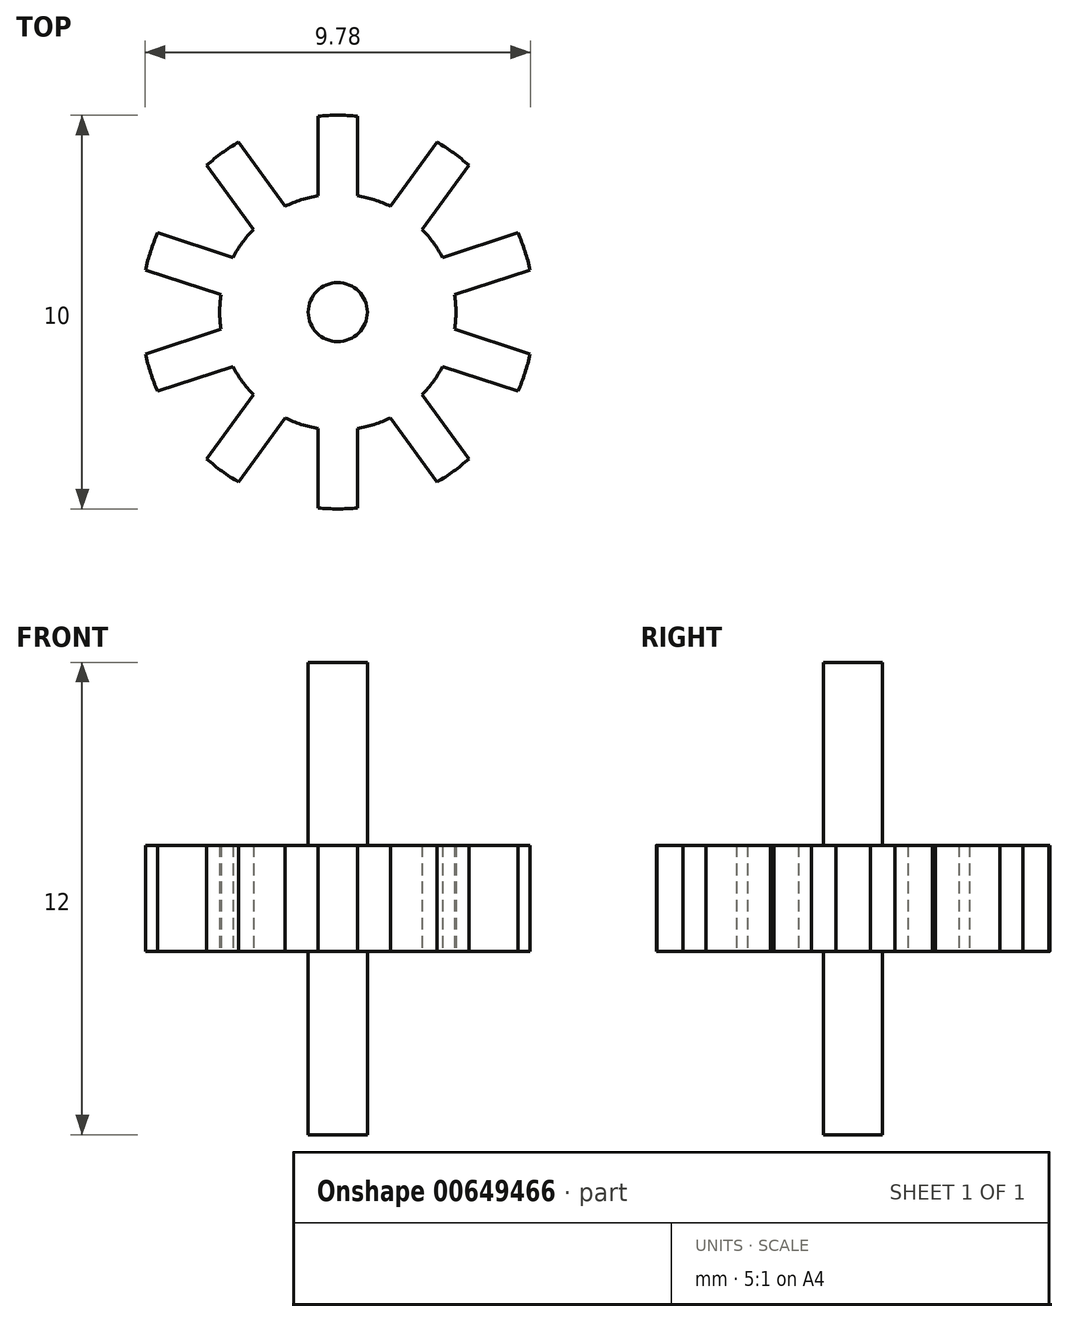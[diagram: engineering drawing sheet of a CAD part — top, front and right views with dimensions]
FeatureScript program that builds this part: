
annotation { "Feature Type Name" : "Feature", "Feature Type Description" : "" }
export const myFeature = defineFeature(function(context is Context, id is Id, definition is map)
    precondition{}
    {
        {
            var Q0;
            Q0=qCreatedBy(makeId("Top.planeOp"),FACE);
            var sketch = newSketch(context, id + "F0", { "sketchPlane" : qUnion([Q0])});
            skCircle(sketch, "E0", {"center": v(0, 0) * mm, "radius": 3 * mm});
            skLineSegment(sketch, "E1.bottom", {"start": v(0.5, 6) * mm, "end": v(-0.5, 6) * mm});
            skLineSegment(sketch, "E1.top", {"start": v(0.5, 0) * mm, "end": v(-0.5, 0) * mm});
            skLineSegment(sketch, "E1.left", {"start": v(0.5, 6) * mm, "end": v(0.5, 0) * mm});
            skLineSegment(sketch, "E1.right", {"start": v(-0.5, 6) * mm, "end": v(-0.5, 0) * mm});
            skPoint(sketch, "E1.middle", {"position": v(0, 3) * mm});
            skLineSegment(sketch, "E2.1.0", {"start": v(-3.12, 5.15) * mm, "end": v(-3.93, 4.56) * mm});
            skLineSegment(sketch, "E2.1.1", {"start": v(-3.93, 4.56) * mm, "end": v(-0.4, -0.3) * mm});
            skLineSegment(sketch, "E2.1.2", {"start": v(-3.12, 5.15) * mm, "end": v(0.4, 0.3) * mm});
            skLineSegment(sketch, "E2.2.0", {"start": v(-5.55, 2.33) * mm, "end": v(-5.86, 1.38) * mm});
            skLineSegment(sketch, "E2.2.1", {"start": v(-5.86, 1.38) * mm, "end": v(-0.15, -0.48) * mm});
            skLineSegment(sketch, "E2.2.2", {"start": v(-5.55, 2.33) * mm, "end": v(0.15, 0.48) * mm});
            skLineSegment(sketch, "E2.3.0", {"start": v(-5.86, -1.38) * mm, "end": v(-5.55, -2.33) * mm});
            skLineSegment(sketch, "E2.3.1", {"start": v(-5.55, -2.33) * mm, "end": v(0.15, -0.48) * mm});
            skLineSegment(sketch, "E2.3.2", {"start": v(-5.86, -1.38) * mm, "end": v(-0.15, 0.48) * mm});
            skLineSegment(sketch, "E2.4.0", {"start": v(-3.93, -4.56) * mm, "end": v(-3.12, -5.15) * mm});
            skLineSegment(sketch, "E2.4.1", {"start": v(-3.12, -5.15) * mm, "end": v(0.4, -0.3) * mm});
            skLineSegment(sketch, "E2.4.2", {"start": v(-3.93, -4.56) * mm, "end": v(-0.4, 0.3) * mm});
            skLineSegment(sketch, "E2.5.0", {"start": v(-0.5, -6) * mm, "end": v(0.5, -6) * mm});
            skLineSegment(sketch, "E2.5.1", {"start": v(0.5, -6) * mm, "end": v(0.5, 0) * mm});
            skLineSegment(sketch, "E2.5.2", {"start": v(-0.5, -6) * mm, "end": v(-0.5, 0) * mm});
            skLineSegment(sketch, "E2.6.0", {"start": v(3.12, -5.15) * mm, "end": v(3.93, -4.56) * mm});
            skLineSegment(sketch, "E2.6.1", {"start": v(3.93, -4.56) * mm, "end": v(0.4, 0.3) * mm});
            skLineSegment(sketch, "E2.6.2", {"start": v(3.12, -5.15) * mm, "end": v(-0.4, -0.3) * mm});
            skLineSegment(sketch, "E2.7.0", {"start": v(5.55, -2.33) * mm, "end": v(5.86, -1.38) * mm});
            skLineSegment(sketch, "E2.7.1", {"start": v(5.86, -1.38) * mm, "end": v(0.15, 0.48) * mm});
            skLineSegment(sketch, "E2.7.2", {"start": v(5.55, -2.33) * mm, "end": v(-0.15, -0.48) * mm});
            skLineSegment(sketch, "E2.8.0", {"start": v(5.86, 1.38) * mm, "end": v(5.55, 2.33) * mm});
            skLineSegment(sketch, "E2.8.1", {"start": v(5.55, 2.33) * mm, "end": v(-0.15, 0.48) * mm});
            skLineSegment(sketch, "E2.8.2", {"start": v(5.86, 1.38) * mm, "end": v(0.15, -0.48) * mm});
            skLineSegment(sketch, "E2.9.0", {"start": v(3.93, 4.56) * mm, "end": v(3.12, 5.15) * mm});
            skLineSegment(sketch, "E2.9.1", {"start": v(3.12, 5.15) * mm, "end": v(-0.4, 0.3) * mm});
            skLineSegment(sketch, "E2.9.2", {"start": v(3.93, 4.56) * mm, "end": v(0.4, -0.3) * mm});
            skCircle(sketch, "E3", {"center": v(0, 0) * mm, "radius": 0.5 * mm});
            skCircle(sketch, "E4", {"center": v(0, 0) * mm, "radius": 5 * mm});
            skSolve(sketch);
        }
        {
            var Q0;
            {var subQ0=sQuery(id+"F0.wireOp",EDGE,"E2.3.2");var subQ1=sQuery(id+"F0.wireOp",EDGE,"E0");var subQ2=makeQuery(id+"F0.imprint","INTERSECT",VERTEX,{"derivedFrom":[subQ1,subQ0]});Q0=makeQuery(id+"F0.imprint","IMPRINT",FACE,{"disambiguationData":[TD([[makeQuery(id+"F0.imprint","IMPRINT",EDGE,{"disambiguationData":[TD([[subQ2,-1.0]])],"derivedFrom":subQ1}),1.0]])]});}
            var Q1;
            {var subQ0=sQuery(id+"F0.wireOp",EDGE,"E2.6.1");var subQ1=sQuery(id+"F0.wireOp",EDGE,"E0");var subQ2=makeQuery(id+"F0.imprint","INTERSECT",VERTEX,{"derivedFrom":[subQ1,subQ0]});Q1=makeQuery(id+"F0.imprint","IMPRINT",FACE,{"disambiguationData":[TD([[makeQuery(id+"F0.imprint","IMPRINT",EDGE,{"disambiguationData":[TD([[subQ2,-1.0]])],"derivedFrom":subQ1}),1.0]])]});}
            var Q2;
            {var subQ0=sQuery(id+"F0.wireOp",EDGE,"E2.4.2");var subQ1=sQuery(id+"F0.wireOp",EDGE,"E0");var subQ2=makeQuery(id+"F0.imprint","INTERSECT",VERTEX,{"derivedFrom":[subQ1,subQ0]});Q2=makeQuery(id+"F0.imprint","IMPRINT",FACE,{"disambiguationData":[TD([[makeQuery(id+"F0.imprint","IMPRINT",EDGE,{"disambiguationData":[TD([[subQ2,-1.0]])],"derivedFrom":subQ1}),1.0]])]});}
            var Q3;
            {var subQ0=sQuery(id+"F0.wireOp",EDGE,"E2.7.1");var subQ1=sQuery(id+"F0.wireOp",EDGE,"E1.left");var subQ2=makeQuery(id+"F0.imprint","INTERSECT",VERTEX,{"derivedFrom":[subQ1,subQ0]});Q3=makeQuery(id+"F0.imprint","IMPRINT",FACE,{"disambiguationData":[TD([[makeQuery(id+"F0.imprint","IMPRINT",EDGE,{"disambiguationData":[TD([[subQ2,-1.0]])],"derivedFrom":subQ1}),1.0]])]});}
            var Q4;
            {var subQ0=sQuery(id+"F0.wireOp",EDGE,"E2.5.1");var subQ1=sQuery(id+"F0.wireOp",EDGE,"E0");var subQ2=makeQuery(id+"F0.imprint","INTERSECT",VERTEX,{"derivedFrom":[subQ1,subQ0]});Q4=makeQuery(id+"F0.imprint","IMPRINT",FACE,{"disambiguationData":[TD([[makeQuery(id+"F0.imprint","IMPRINT",EDGE,{"disambiguationData":[TD([[subQ2,-1.0]])],"derivedFrom":subQ1}),1.0]])]});}
            var Q5;
            {var subQ4=sQuery(id+"F0.wireOp",EDGE,"E1.top");Q5=makeQuery(id+"F0.imprint","IMPRINT",FACE,{"disambiguationData":[TD([[makeQuery(id+"F0.imprint","IMPRINT",EDGE,{"derivedFrom":subQ4}),1.0]])]});}
            var Q6;
            {var subQ0=sQuery(id+"F0.wireOp",EDGE,"E2.3.2");var subQ1=sQuery(id+"F0.wireOp",EDGE,"E1.right");var subQ2=makeQuery(id+"F0.imprint","INTERSECT",VERTEX,{"derivedFrom":[subQ1,subQ0]});Q6=makeQuery(id+"F0.imprint","IMPRINT",FACE,{"disambiguationData":[TD([[makeQuery(id+"F0.imprint","IMPRINT",EDGE,{"disambiguationData":[TD([[subQ2,-1.0]])],"derivedFrom":subQ1}),-1.0]])]});}
            var Q7;
            {var subQ0=sQuery(id+"F0.wireOp",EDGE,"E2.7.2");var subQ1=sQuery(id+"F0.wireOp",EDGE,"E2.4.1");var subQ2=makeQuery(id+"F0.imprint","INTERSECT",VERTEX,{"derivedFrom":[subQ1,subQ0]});Q7=makeQuery(id+"F0.imprint","IMPRINT",FACE,{"disambiguationData":[TD([[makeQuery(id+"F0.imprint","IMPRINT",EDGE,{"disambiguationData":[TD([[subQ2,-1.0]])],"derivedFrom":subQ1}),-1.0]])]});}
            var Q8;
            {var subQ0=sQuery(id+"F0.wireOp",EDGE,"E1.right");var subQ1=sQuery(id+"F0.wireOp",EDGE,"E0");var subQ2=makeQuery(id+"F0.imprint","INTERSECT",VERTEX,{"derivedFrom":[subQ1,subQ0]});Q8=makeQuery(id+"F0.imprint","IMPRINT",FACE,{"disambiguationData":[TD([[makeQuery(id+"F0.imprint","IMPRINT",EDGE,{"disambiguationData":[TD([[subQ2,-1.0]])],"derivedFrom":subQ1}),1.0]])]});}
            var Q9;
            {var subQ0=sQuery(id+"F0.wireOp",EDGE,"E2.9.1");var subQ1=sQuery(id+"F0.wireOp",EDGE,"E0");var subQ2=makeQuery(id+"F0.imprint","INTERSECT",VERTEX,{"derivedFrom":[subQ1,subQ0]});Q9=makeQuery(id+"F0.imprint","IMPRINT",FACE,{"disambiguationData":[TD([[makeQuery(id+"F0.imprint","IMPRINT",EDGE,{"disambiguationData":[TD([[subQ2,-1.0]])],"derivedFrom":subQ1}),1.0]])]});}
            var Q10;
            {var subQ0=sQuery(id+"F0.wireOp",EDGE,"E2.8.1");var subQ1=sQuery(id+"F0.wireOp",EDGE,"E0");var subQ2=makeQuery(id+"F0.imprint","INTERSECT",VERTEX,{"derivedFrom":[subQ1,subQ0]});Q10=makeQuery(id+"F0.imprint","IMPRINT",FACE,{"disambiguationData":[TD([[makeQuery(id+"F0.imprint","IMPRINT",EDGE,{"disambiguationData":[TD([[subQ2,-1.0]])],"derivedFrom":subQ1}),1.0]])]});}
            var Q11;
            {var subQ0=sQuery(id+"F0.wireOp",EDGE,"E2.8.1");var subQ1=sQuery(id+"F0.wireOp",EDGE,"E1.left");var subQ2=makeQuery(id+"F0.imprint","INTERSECT",VERTEX,{"derivedFrom":[subQ1,subQ0]});Q11=makeQuery(id+"F0.imprint","IMPRINT",FACE,{"disambiguationData":[TD([[makeQuery(id+"F0.imprint","IMPRINT",EDGE,{"disambiguationData":[TD([[subQ2,-1.0]])],"derivedFrom":subQ1}),1.0]])]});}
            var Q12;
            {var subQ0=sQuery(id+"F0.wireOp",EDGE,"E2.5.2");var subQ1=sQuery(id+"F0.wireOp",EDGE,"E2.2.1");var subQ2=makeQuery(id+"F0.imprint","INTERSECT",VERTEX,{"derivedFrom":[subQ1,subQ0]});Q12=makeQuery(id+"F0.imprint","IMPRINT",FACE,{"disambiguationData":[TD([[makeQuery(id+"F0.imprint","IMPRINT",EDGE,{"disambiguationData":[TD([[subQ2,-1.0]])],"derivedFrom":subQ1}),-1.0]])]});}
            var Q13;
            {var subQ0=sQuery(id+"F0.wireOp",EDGE,"E2.2.2");var subQ1=sQuery(id+"F0.wireOp",EDGE,"E0");var subQ2=makeQuery(id+"F0.imprint","INTERSECT",VERTEX,{"derivedFrom":[subQ1,subQ0]});Q13=makeQuery(id+"F0.imprint","IMPRINT",FACE,{"disambiguationData":[TD([[makeQuery(id+"F0.imprint","IMPRINT",EDGE,{"disambiguationData":[TD([[subQ2,-1.0]])],"derivedFrom":subQ1}),1.0]])]});}
            var Q14;
            {var subQ0=sQuery(id+"F0.wireOp",EDGE,"E2.2.1");var subQ1=sQuery(id+"F0.wireOp",EDGE,"E0");var subQ2=makeQuery(id+"F0.imprint","INTERSECT",VERTEX,{"derivedFrom":[subQ1,subQ0]});Q14=makeQuery(id+"F0.imprint","IMPRINT",FACE,{"disambiguationData":[TD([[makeQuery(id+"F0.imprint","IMPRINT",EDGE,{"disambiguationData":[TD([[subQ2,-1.0]])],"derivedFrom":subQ1}),1.0]])]});}
            var Q15;
            {var subQ0=sQuery(id+"F0.wireOp",EDGE,"E2.4.1");var subQ1=sQuery(id+"F0.wireOp",EDGE,"E0");var subQ2=makeQuery(id+"F0.imprint","INTERSECT",VERTEX,{"derivedFrom":[subQ1,subQ0]});Q15=makeQuery(id+"F0.imprint","IMPRINT",FACE,{"disambiguationData":[TD([[makeQuery(id+"F0.imprint","IMPRINT",EDGE,{"disambiguationData":[TD([[subQ2,-1.0]])],"derivedFrom":subQ1}),1.0]])]});}
            var Q16;
            {var subQ0=sQuery(id+"F0.wireOp",EDGE,"E2.1.1");var subQ1=sQuery(id+"F0.wireOp",EDGE,"E0");var subQ2=makeQuery(id+"F0.imprint","INTERSECT",VERTEX,{"derivedFrom":[subQ1,subQ0]});Q16=makeQuery(id+"F0.imprint","IMPRINT",FACE,{"disambiguationData":[TD([[makeQuery(id+"F0.imprint","IMPRINT",EDGE,{"disambiguationData":[TD([[subQ2,-1.0]])],"derivedFrom":subQ1}),1.0]])]});}
            var Q17;
            {var subQ0=sQuery(id+"F0.wireOp",EDGE,"E2.3.1");var subQ1=sQuery(id+"F0.wireOp",EDGE,"E0");var subQ2=makeQuery(id+"F0.imprint","INTERSECT",VERTEX,{"derivedFrom":[subQ1,subQ0]});Q17=makeQuery(id+"F0.imprint","IMPRINT",FACE,{"disambiguationData":[TD([[makeQuery(id+"F0.imprint","IMPRINT",EDGE,{"disambiguationData":[TD([[subQ2,-1.0]])],"derivedFrom":subQ1}),1.0]])]});}
            var Q18;
            {var subQ0=sQuery(id+"F0.wireOp",EDGE,"E2.2.2");var subQ1=sQuery(id+"F0.wireOp",EDGE,"E1.right");var subQ2=makeQuery(id+"F0.imprint","INTERSECT",VERTEX,{"derivedFrom":[subQ1,subQ0]});Q18=makeQuery(id+"F0.imprint","IMPRINT",FACE,{"disambiguationData":[TD([[makeQuery(id+"F0.imprint","IMPRINT",EDGE,{"disambiguationData":[TD([[subQ2,-1.0]])],"derivedFrom":subQ1}),1.0]])]});}
            var Q19;
            {var subQ0=sQuery(id+"F0.wireOp",EDGE,"E2.6.2");var subQ1=sQuery(id+"F0.wireOp",EDGE,"E2.4.1");var subQ2=makeQuery(id+"F0.imprint","INTERSECT",VERTEX,{"derivedFrom":[subQ1,subQ0]});Q19=makeQuery(id+"F0.imprint","IMPRINT",FACE,{"disambiguationData":[TD([[makeQuery(id+"F0.imprint","IMPRINT",EDGE,{"disambiguationData":[TD([[subQ2,-1.0]])],"derivedFrom":subQ1}),-1.0]])]});}
            var Q20;
            {var subQ4=sQuery(id+"F0.wireOp",EDGE,"E1.top");Q20=makeQuery(id+"F0.imprint","IMPRINT",FACE,{"disambiguationData":[TD([[makeQuery(id+"F0.imprint","IMPRINT",EDGE,{"derivedFrom":subQ4}),-1.0]])]});}
            var Q21;
            {var subQ1=sQuery(id+"F0.wireOp",EDGE,"E0");var subQ5=sQuery(id+"F0.wireOp",EDGE,"E2.8.1");var subQ6=makeQuery(id+"F0.imprint","INTERSECT",VERTEX,{"derivedFrom":[subQ1,subQ5]});Q21=makeQuery(id+"F0.imprint","IMPRINT",FACE,{"disambiguationData":[TD([[makeQuery(id+"F0.imprint","IMPRINT",EDGE,{"disambiguationData":[TD([[subQ6,1.0]])],"derivedFrom":subQ1}),1.0]])]});}
            var Q22;
            {var subQ0=sQuery(id+"F0.wireOp",EDGE,"E2.9.1");var subQ1=sQuery(id+"F0.wireOp",EDGE,"E1.left");var subQ2=makeQuery(id+"F0.imprint","INTERSECT",VERTEX,{"derivedFrom":[subQ1,subQ0]});Q22=makeQuery(id+"F0.imprint","IMPRINT",FACE,{"disambiguationData":[TD([[makeQuery(id+"F0.imprint","IMPRINT",EDGE,{"disambiguationData":[TD([[subQ2,-1.0]])],"derivedFrom":subQ1}),-1.0]])]});}
            var Q23;
            {var subQ0=sQuery(id+"F0.wireOp",EDGE,"E2.2.2");var subQ1=sQuery(id+"F0.wireOp",EDGE,"E1.right");var subQ2=makeQuery(id+"F0.imprint","INTERSECT",VERTEX,{"derivedFrom":[subQ1,subQ0]});Q23=makeQuery(id+"F0.imprint","IMPRINT",FACE,{"disambiguationData":[TD([[makeQuery(id+"F0.imprint","IMPRINT",EDGE,{"disambiguationData":[TD([[subQ2,-1.0]])],"derivedFrom":subQ1}),-1.0]])]});}
            var Q24;
            {var subQ5=sQuery(id+"F0.wireOp",EDGE,"E0");var subQ7=sQuery(id+"F0.wireOp",EDGE,"E1.left");var subQ8=makeQuery(id+"F0.imprint","INTERSECT",VERTEX,{"derivedFrom":[subQ5,subQ7]});Q24=makeQuery(id+"F0.imprint","IMPRINT",FACE,{"disambiguationData":[TD([[makeQuery(id+"F0.imprint","IMPRINT",EDGE,{"disambiguationData":[TD([[subQ8,-1.0]])],"derivedFrom":subQ5}),1.0]])]});}
            var Q25;
            {var subQ0=sQuery(id+"F0.wireOp",EDGE,"E2.7.2");var subQ1=sQuery(id+"F0.wireOp",EDGE,"E0");var subQ2=makeQuery(id+"F0.imprint","INTERSECT",VERTEX,{"derivedFrom":[subQ1,subQ0]});Q25=makeQuery(id+"F0.imprint","IMPRINT",FACE,{"disambiguationData":[TD([[makeQuery(id+"F0.imprint","IMPRINT",EDGE,{"disambiguationData":[TD([[subQ2,-1.0]])],"derivedFrom":subQ1}),1.0]])]});}
            var Q26;
            {var subQ0=sQuery(id+"F0.wireOp",EDGE,"E2.4.2");var subQ1=sQuery(id+"F0.wireOp",EDGE,"E2.1.1");var subQ2=makeQuery(id+"F0.imprint","INTERSECT",VERTEX,{"derivedFrom":[subQ1,subQ0]});Q26=makeQuery(id+"F0.imprint","IMPRINT",FACE,{"disambiguationData":[TD([[makeQuery(id+"F0.imprint","IMPRINT",EDGE,{"disambiguationData":[TD([[subQ2,-1.0]])],"derivedFrom":subQ1}),-1.0]])]});}
            var Q27;
            {var subQ0=sQuery(id+"F0.wireOp",EDGE,"E2.8.2");var subQ1=sQuery(id+"F0.wireOp",EDGE,"E2.6.1");var subQ2=makeQuery(id+"F0.imprint","INTERSECT",VERTEX,{"derivedFrom":[subQ1,subQ0]});Q27=makeQuery(id+"F0.imprint","IMPRINT",FACE,{"disambiguationData":[TD([[makeQuery(id+"F0.imprint","IMPRINT",EDGE,{"disambiguationData":[TD([[subQ2,-1.0]])],"derivedFrom":subQ1}),-1.0]])]});}
            var Q28;
            {var subQ0=sQuery(id+"F0.wireOp",EDGE,"E2.1.2");var subQ1=sQuery(id+"F0.wireOp",EDGE,"E1.right");var subQ2=makeQuery(id+"F0.imprint","INTERSECT",VERTEX,{"derivedFrom":[subQ1,subQ0]});Q28=makeQuery(id+"F0.imprint","IMPRINT",FACE,{"disambiguationData":[TD([[makeQuery(id+"F0.imprint","IMPRINT",EDGE,{"disambiguationData":[TD([[subQ2,-1.0]])],"derivedFrom":subQ1}),1.0]])]});}
            var Q29;
            {var subQ0=sQuery(id+"F0.wireOp",EDGE,"E2.6.2");var subQ1=sQuery(id+"F0.wireOp",EDGE,"E2.3.1");var subQ2=makeQuery(id+"F0.imprint","INTERSECT",VERTEX,{"derivedFrom":[subQ1,subQ0]});Q29=makeQuery(id+"F0.imprint","IMPRINT",FACE,{"disambiguationData":[TD([[makeQuery(id+"F0.imprint","IMPRINT",EDGE,{"disambiguationData":[TD([[subQ2,-1.0]])],"derivedFrom":subQ1}),-1.0]])]});}
            var Q30;
            {var subQ0=sQuery(id+"F0.wireOp",EDGE,"E2.9.1");var subQ1=sQuery(id+"F0.wireOp",EDGE,"E2.1.2");var subQ2=makeQuery(id+"F0.imprint","INTERSECT",VERTEX,{"derivedFrom":[subQ1,subQ0]});Q30=makeQuery(id+"F0.imprint","IMPRINT",FACE,{"disambiguationData":[TD([[makeQuery(id+"F0.imprint","IMPRINT",EDGE,{"disambiguationData":[TD([[subQ2,-1.0]])],"derivedFrom":subQ1}),-1.0]])]});}
            var Q31;
            {var subQ1=sQuery(id+"F0.wireOp",EDGE,"E0");var subQ5=sQuery(id+"F0.wireOp",EDGE,"E2.6.2");var subQ9=makeQuery(id+"F0.imprint","INTERSECT",VERTEX,{"derivedFrom":[subQ1,subQ5]});Q31=makeQuery(id+"F0.imprint","IMPRINT",FACE,{"disambiguationData":[TD([[makeQuery(id+"F0.imprint","IMPRINT",EDGE,{"disambiguationData":[TD([[subQ9,-1.0]])],"derivedFrom":subQ1}),1.0]])]});}
            var Q32;
            {var subQ1=sQuery(id+"F0.wireOp",EDGE,"E0");var subQ7=sQuery(id+"F0.wireOp",EDGE,"E2.9.2");var subQ9=makeQuery(id+"F0.imprint","INTERSECT",VERTEX,{"derivedFrom":[subQ1,subQ7]});Q32=makeQuery(id+"F0.imprint","IMPRINT",FACE,{"disambiguationData":[TD([[makeQuery(id+"F0.imprint","IMPRINT",EDGE,{"disambiguationData":[TD([[subQ9,-1.0]])],"derivedFrom":subQ1}),1.0]])]});}
            var Q33;
            {var subQ0=sQuery(id+"F0.wireOp",EDGE,"E2.3.2");var subQ1=sQuery(id+"F0.wireOp",EDGE,"E2.1.1");var subQ2=makeQuery(id+"F0.imprint","INTERSECT",VERTEX,{"derivedFrom":[subQ1,subQ0]});Q33=makeQuery(id+"F0.imprint","IMPRINT",FACE,{"disambiguationData":[TD([[makeQuery(id+"F0.imprint","IMPRINT",EDGE,{"disambiguationData":[TD([[subQ2,-1.0]])],"derivedFrom":subQ1}),-1.0]])]});}
            var Q34;
            {var subQ0=sQuery(id+"F0.wireOp",EDGE,"E2.8.2");var subQ1=sQuery(id+"F0.wireOp",EDGE,"E2.5.1");var subQ2=makeQuery(id+"F0.imprint","INTERSECT",VERTEX,{"derivedFrom":[subQ1,subQ0]});Q34=makeQuery(id+"F0.imprint","IMPRINT",FACE,{"disambiguationData":[TD([[makeQuery(id+"F0.imprint","IMPRINT",EDGE,{"disambiguationData":[TD([[subQ2,-1.0]])],"derivedFrom":subQ1}),-1.0]])]});}
            var Q35;
            {var subQ0=sQuery(id+"F0.wireOp",EDGE,"E2.5.2");var subQ1=sQuery(id+"F0.wireOp",EDGE,"E2.3.1");var subQ2=makeQuery(id+"F0.imprint","INTERSECT",VERTEX,{"derivedFrom":[subQ1,subQ0]});Q35=makeQuery(id+"F0.imprint","IMPRINT",FACE,{"disambiguationData":[TD([[makeQuery(id+"F0.imprint","IMPRINT",EDGE,{"disambiguationData":[TD([[subQ2,-1.0]])],"derivedFrom":subQ1}),-1.0]])]});}
            var Q36;
            {var subQ0=sQuery(id+"F0.wireOp",EDGE,"E2.5.2");var subQ1=sQuery(id+"F0.wireOp",EDGE,"E0");var subQ2=makeQuery(id+"F0.imprint","INTERSECT",VERTEX,{"derivedFrom":[subQ1,subQ0]});Q36=makeQuery(id+"F0.imprint","IMPRINT",FACE,{"disambiguationData":[TD([[makeQuery(id+"F0.imprint","IMPRINT",EDGE,{"disambiguationData":[TD([[subQ2,-1.0]])],"derivedFrom":subQ1}),1.0]])]});}
            var Q37;
            {var subQ0=sQuery(id+"F0.wireOp",EDGE,"E2.8.2");var subQ1=sQuery(id+"F0.wireOp",EDGE,"E0");var subQ2=makeQuery(id+"F0.imprint","INTERSECT",VERTEX,{"derivedFrom":[subQ1,subQ0]});Q37=makeQuery(id+"F0.imprint","IMPRINT",FACE,{"disambiguationData":[TD([[makeQuery(id+"F0.imprint","IMPRINT",EDGE,{"disambiguationData":[TD([[subQ2,1.0]])],"derivedFrom":subQ1}),1.0]])]});}
            var Q38;
            {var subQ0=sQuery(id+"F0.wireOp",EDGE,"E2.7.2");var subQ1=sQuery(id+"F0.wireOp",EDGE,"E2.5.1");var subQ2=makeQuery(id+"F0.imprint","INTERSECT",VERTEX,{"derivedFrom":[subQ1,subQ0]});Q38=makeQuery(id+"F0.imprint","IMPRINT",FACE,{"disambiguationData":[TD([[makeQuery(id+"F0.imprint","IMPRINT",EDGE,{"disambiguationData":[TD([[subQ2,-1.0]])],"derivedFrom":subQ1}),-1.0]])]});}
            var Q39;
            {var subQ0=sQuery(id+"F0.wireOp",EDGE,"E2.8.1");var subQ1=sQuery(id+"F0.wireOp",EDGE,"E1.left");var subQ2=makeQuery(id+"F0.imprint","INTERSECT",VERTEX,{"derivedFrom":[subQ1,subQ0]});Q39=makeQuery(id+"F0.imprint","IMPRINT",FACE,{"disambiguationData":[TD([[makeQuery(id+"F0.imprint","IMPRINT",EDGE,{"disambiguationData":[TD([[subQ2,-1.0]])],"derivedFrom":subQ1}),-1.0]])]});}
            var Q40;
            {var subQ1=sQuery(id+"F0.wireOp",EDGE,"E0");var subQ5=sQuery(id+"F0.wireOp",EDGE,"E2.1.2");var subQ6=makeQuery(id+"F0.imprint","INTERSECT",VERTEX,{"derivedFrom":[subQ1,subQ5]});Q40=makeQuery(id+"F0.imprint","IMPRINT",FACE,{"disambiguationData":[TD([[makeQuery(id+"F0.imprint","IMPRINT",EDGE,{"disambiguationData":[TD([[subQ6,-1.0]])],"derivedFrom":subQ1}),1.0]])]});}
            var Q41;
            {var subQ0=sQuery(id+"F0.wireOp",EDGE,"E2.4.2");var subQ1=sQuery(id+"F0.wireOp",EDGE,"E2.2.1");var subQ2=makeQuery(id+"F0.imprint","INTERSECT",VERTEX,{"derivedFrom":[subQ1,subQ0]});Q41=makeQuery(id+"F0.imprint","IMPRINT",FACE,{"disambiguationData":[TD([[makeQuery(id+"F0.imprint","IMPRINT",EDGE,{"disambiguationData":[TD([[subQ2,-1.0]])],"derivedFrom":subQ1}),-1.0]])]});}
            var Q42;
            {var subQ3=sQuery(id+"F0.wireOp",EDGE,"E2.6.2");var subQ5=sQuery(id+"F0.wireOp",EDGE,"E2.3.1");var subQ6=makeQuery(id+"F0.imprint","INTERSECT",VERTEX,{"derivedFrom":[subQ5,subQ3]});Q42=makeQuery(id+"F0.imprint","IMPRINT",FACE,{"disambiguationData":[TD([[makeQuery(id+"F0.imprint","IMPRINT",EDGE,{"disambiguationData":[TD([[subQ6,-1.0]])],"derivedFrom":subQ5}),1.0]])]});}
            var Q43;
            {var subQ3=sQuery(id+"F0.wireOp",EDGE,"E2.8.2");var subQ5=sQuery(id+"F0.wireOp",EDGE,"E2.5.1");var subQ6=makeQuery(id+"F0.imprint","INTERSECT",VERTEX,{"derivedFrom":[subQ5,subQ3]});Q43=makeQuery(id+"F0.imprint","IMPRINT",FACE,{"disambiguationData":[TD([[makeQuery(id+"F0.imprint","IMPRINT",EDGE,{"disambiguationData":[TD([[subQ6,-1.0]])],"derivedFrom":subQ5}),1.0]])]});}
            var Q44;
            {var subQ0=sQuery(id+"F0.wireOp",EDGE,"E2.9.1");var subQ1=sQuery(id+"F0.wireOp",EDGE,"E2.2.2");var subQ2=makeQuery(id+"F0.imprint","INTERSECT",VERTEX,{"derivedFrom":[subQ1,subQ0]});Q44=makeQuery(id+"F0.imprint","IMPRINT",FACE,{"disambiguationData":[TD([[makeQuery(id+"F0.imprint","IMPRINT",EDGE,{"disambiguationData":[TD([[subQ2,-1.0]])],"derivedFrom":subQ1}),-1.0]])]});}
            var Q45;
            {var subQ3=sQuery(id+"F0.wireOp",EDGE,"E2.5.2");var subQ5=sQuery(id+"F0.wireOp",EDGE,"E2.2.1");var subQ6=makeQuery(id+"F0.imprint","INTERSECT",VERTEX,{"derivedFrom":[subQ5,subQ3]});Q45=makeQuery(id+"F0.imprint","IMPRINT",FACE,{"disambiguationData":[TD([[makeQuery(id+"F0.imprint","IMPRINT",EDGE,{"disambiguationData":[TD([[subQ6,-1.0]])],"derivedFrom":subQ5}),1.0]])]});}
            var Q46;
            {var subQ0=sQuery(id+"F0.wireOp",EDGE,"E2.8.1");var subQ1=sQuery(id+"F0.wireOp",EDGE,"E2.1.2");var subQ2=makeQuery(id+"F0.imprint","INTERSECT",VERTEX,{"derivedFrom":[subQ1,subQ0]});Q46=makeQuery(id+"F0.imprint","IMPRINT",FACE,{"disambiguationData":[TD([[makeQuery(id+"F0.imprint","IMPRINT",EDGE,{"disambiguationData":[TD([[subQ2,-1.0]])],"derivedFrom":subQ1}),-1.0]])]});}
            var Q47;
            {var subQ3=sQuery(id+"F0.wireOp",EDGE,"E2.7.2");var subQ5=sQuery(id+"F0.wireOp",EDGE,"E2.4.1");var subQ6=makeQuery(id+"F0.imprint","INTERSECT",VERTEX,{"derivedFrom":[subQ5,subQ3]});Q47=makeQuery(id+"F0.imprint","IMPRINT",FACE,{"disambiguationData":[TD([[makeQuery(id+"F0.imprint","IMPRINT",EDGE,{"disambiguationData":[TD([[subQ6,-1.0]])],"derivedFrom":subQ5}),1.0]])]});}
            var Q48;
            {var subQ1=sQuery(id+"F0.wireOp",EDGE,"E1.right");var subQ3=sQuery(id+"F0.wireOp",EDGE,"E2.4.2");var subQ4=makeQuery(id+"F0.imprint","INTERSECT",VERTEX,{"derivedFrom":[subQ1,subQ3]});Q48=makeQuery(id+"F0.imprint","IMPRINT",FACE,{"disambiguationData":[TD([[makeQuery(id+"F0.imprint","IMPRINT",EDGE,{"disambiguationData":[TD([[subQ4,-1.0]])],"derivedFrom":subQ3}),-1.0]])]});}
            var Q49;
            {var subQ1=sQuery(id+"F0.wireOp",EDGE,"E1.left");var subQ3=sQuery(id+"F0.wireOp",EDGE,"E2.6.1");var subQ4=makeQuery(id+"F0.imprint","INTERSECT",VERTEX,{"derivedFrom":[subQ1,subQ3]});Q49=makeQuery(id+"F0.imprint","IMPRINT",FACE,{"disambiguationData":[TD([[makeQuery(id+"F0.imprint","IMPRINT",EDGE,{"disambiguationData":[TD([[subQ4,1.0]])],"derivedFrom":subQ3}),1.0]])]});}
            var Q50;
            {var subQ0=sQuery(id+"F0.wireOp",EDGE,"E2.7.1");var subQ1=sQuery(id+"F0.wireOp",EDGE,"E1.left");var subQ2=makeQuery(id+"F0.imprint","INTERSECT",VERTEX,{"derivedFrom":[subQ1,subQ0]});Q50=makeQuery(id+"F0.imprint","IMPRINT",FACE,{"disambiguationData":[TD([[makeQuery(id+"F0.imprint","IMPRINT",EDGE,{"disambiguationData":[TD([[subQ2,-1.0]])],"derivedFrom":subQ1}),-1.0]])]});}
            var Q51;
            {var subQ1=sQuery(id+"F0.wireOp",EDGE,"E2.2.1");var subQ3=sQuery(id+"F0.wireOp",EDGE,"E2.6.2");var subQ4=makeQuery(id+"F0.imprint","INTERSECT",VERTEX,{"derivedFrom":[subQ1,subQ3]});Q51=makeQuery(id+"F0.imprint","IMPRINT",FACE,{"disambiguationData":[TD([[makeQuery(id+"F0.imprint","IMPRINT",EDGE,{"disambiguationData":[TD([[subQ4,-1.0]])],"derivedFrom":subQ1}),1.0]])]});}
            var Q52;
            {var subQ0=sQuery(id+"F0.wireOp",EDGE,"E2.3.2");var subQ1=sQuery(id+"F0.wireOp",EDGE,"E1.right");var subQ2=makeQuery(id+"F0.imprint","INTERSECT",VERTEX,{"derivedFrom":[subQ1,subQ0]});Q52=makeQuery(id+"F0.imprint","IMPRINT",FACE,{"disambiguationData":[TD([[makeQuery(id+"F0.imprint","IMPRINT",EDGE,{"disambiguationData":[TD([[subQ2,-1.0]])],"derivedFrom":subQ1}),1.0]])]});}
            var Q53;
            {var subQ1=sQuery(id+"F0.wireOp",EDGE,"E2.1.2");var subQ3=sQuery(id+"F0.wireOp",EDGE,"E2.7.1");var subQ4=makeQuery(id+"F0.imprint","INTERSECT",VERTEX,{"derivedFrom":[subQ1,subQ3]});Q53=makeQuery(id+"F0.imprint","IMPRINT",FACE,{"disambiguationData":[TD([[makeQuery(id+"F0.imprint","IMPRINT",EDGE,{"disambiguationData":[TD([[subQ4,-1.0]])],"derivedFrom":subQ1}),-1.0]])]});}
            var Q54;
            {var subQ1=sQuery(id+"F0.wireOp",EDGE,"E2.1.1");var subQ3=sQuery(id+"F0.wireOp",EDGE,"E2.5.2");var subQ4=makeQuery(id+"F0.imprint","INTERSECT",VERTEX,{"derivedFrom":[subQ1,subQ3]});Q54=makeQuery(id+"F0.imprint","IMPRINT",FACE,{"disambiguationData":[TD([[makeQuery(id+"F0.imprint","IMPRINT",EDGE,{"disambiguationData":[TD([[subQ4,-1.0]])],"derivedFrom":subQ1}),1.0]])]});}
            var Q55;
            {var subQ1=sQuery(id+"F0.wireOp",EDGE,"E2.4.1");var subQ3=sQuery(id+"F0.wireOp",EDGE,"E2.8.2");var subQ4=makeQuery(id+"F0.imprint","INTERSECT",VERTEX,{"derivedFrom":[subQ1,subQ3]});Q55=makeQuery(id+"F0.imprint","IMPRINT",FACE,{"disambiguationData":[TD([[makeQuery(id+"F0.imprint","IMPRINT",EDGE,{"disambiguationData":[TD([[subQ4,-1.0]])],"derivedFrom":subQ1}),1.0]])]});}
            var Q56;
            {var subQ1=sQuery(id+"F0.wireOp",EDGE,"E2.3.2");var subQ3=sQuery(id+"F0.wireOp",EDGE,"E2.9.1");var subQ4=makeQuery(id+"F0.imprint","INTERSECT",VERTEX,{"derivedFrom":[subQ1,subQ3]});Q56=makeQuery(id+"F0.imprint","IMPRINT",FACE,{"disambiguationData":[TD([[makeQuery(id+"F0.imprint","IMPRINT",EDGE,{"disambiguationData":[TD([[subQ4,-1.0]])],"derivedFrom":subQ1}),-1.0]])]});}
            var Q57;
            {var subQ1=sQuery(id+"F0.wireOp",EDGE,"E2.5.1");var subQ3=sQuery(id+"F0.wireOp",EDGE,"E2.9.2");var subQ4=makeQuery(id+"F0.imprint","INTERSECT",VERTEX,{"derivedFrom":[subQ1,subQ3]});Q57=makeQuery(id+"F0.imprint","IMPRINT",FACE,{"disambiguationData":[TD([[makeQuery(id+"F0.imprint","IMPRINT",EDGE,{"disambiguationData":[TD([[subQ4,-1.0]])],"derivedFrom":subQ3}),-1.0]])]});}
            var Q58;
            {var subQ1=sQuery(id+"F0.wireOp",EDGE,"E1.left");var subQ3=sQuery(id+"F0.wireOp",EDGE,"E2.6.1");var subQ4=makeQuery(id+"F0.imprint","INTERSECT",VERTEX,{"derivedFrom":[subQ1,subQ3]});Q58=makeQuery(id+"F0.imprint","IMPRINT",FACE,{"disambiguationData":[TD([[makeQuery(id+"F0.imprint","IMPRINT",EDGE,{"disambiguationData":[TD([[subQ4,-1.0]])],"derivedFrom":subQ3}),1.0]])]});}
            var Q59;
            {var subQ1=sQuery(id+"F0.wireOp",EDGE,"E2.3.1");var subQ3=sQuery(id+"F0.wireOp",EDGE,"E2.7.2");var subQ4=makeQuery(id+"F0.imprint","INTERSECT",VERTEX,{"derivedFrom":[subQ1,subQ3]});Q59=makeQuery(id+"F0.imprint","IMPRINT",FACE,{"disambiguationData":[TD([[makeQuery(id+"F0.imprint","IMPRINT",EDGE,{"disambiguationData":[TD([[subQ4,-1.0]])],"derivedFrom":subQ1}),1.0]])]});}
            var Q60;
            {var subQ1=sQuery(id+"F0.wireOp",EDGE,"E2.2.2");var subQ3=sQuery(id+"F0.wireOp",EDGE,"E2.8.1");var subQ4=makeQuery(id+"F0.imprint","INTERSECT",VERTEX,{"derivedFrom":[subQ1,subQ3]});Q60=makeQuery(id+"F0.imprint","IMPRINT",FACE,{"disambiguationData":[TD([[makeQuery(id+"F0.imprint","IMPRINT",EDGE,{"disambiguationData":[TD([[subQ4,-1.0]])],"derivedFrom":subQ1}),-1.0]])]});}
            var Q61;
            {var subQ3=sQuery(id+"F0.wireOp",EDGE,"E2.4.2");var subQ5=sQuery(id+"F0.wireOp",EDGE,"E2.1.1");var subQ7=makeQuery(id+"F0.imprint","INTERSECT",VERTEX,{"derivedFrom":[subQ5,subQ3]});Q61=makeQuery(id+"F0.imprint","IMPRINT",FACE,{"disambiguationData":[TD([[makeQuery(id+"F0.imprint","IMPRINT",EDGE,{"disambiguationData":[TD([[subQ7,-1.0]])],"derivedFrom":subQ5}),1.0]])]});}
            var Q62;
            {var subQ0=sQuery(id+"F0.wireOp",EDGE,"E2.1.2");var subQ1=sQuery(id+"F0.wireOp",EDGE,"E0");var subQ2=makeQuery(id+"F0.imprint","INTERSECT",VERTEX,{"derivedFrom":[subQ1,subQ0]});Q62=makeQuery(id+"F0.imprint","IMPRINT",FACE,{"disambiguationData":[TD([[makeQuery(id+"F0.imprint","IMPRINT",EDGE,{"disambiguationData":[TD([[subQ2,-1.0]])],"derivedFrom":subQ1}),-1.0]])]});}
            var Q63;
            {var subQ0=sQuery(id+"F0.wireOp",EDGE,"E1.left");var subQ1=sQuery(id+"F0.wireOp",EDGE,"E0");var subQ2=makeQuery(id+"F0.imprint","INTERSECT",VERTEX,{"derivedFrom":[subQ1,subQ0]});Q63=makeQuery(id+"F0.imprint","IMPRINT",FACE,{"disambiguationData":[TD([[makeQuery(id+"F0.imprint","IMPRINT",EDGE,{"disambiguationData":[TD([[subQ2,-1.0]])],"derivedFrom":subQ1}),-1.0]])]});}
            var Q64;
            {var subQ0=sQuery(id+"F0.wireOp",EDGE,"E2.9.2");var subQ1=sQuery(id+"F0.wireOp",EDGE,"E0");var subQ2=makeQuery(id+"F0.imprint","INTERSECT",VERTEX,{"derivedFrom":[subQ1,subQ0]});Q64=makeQuery(id+"F0.imprint","IMPRINT",FACE,{"disambiguationData":[TD([[makeQuery(id+"F0.imprint","IMPRINT",EDGE,{"disambiguationData":[TD([[subQ2,-1.0]])],"derivedFrom":subQ1}),-1.0]])]});}
            var Q65;
            {var subQ0=sQuery(id+"F0.wireOp",EDGE,"E2.8.1");var subQ1=sQuery(id+"F0.wireOp",EDGE,"E0");var subQ2=makeQuery(id+"F0.imprint","INTERSECT",VERTEX,{"derivedFrom":[subQ1,subQ0]});Q65=makeQuery(id+"F0.imprint","IMPRINT",FACE,{"disambiguationData":[TD([[makeQuery(id+"F0.imprint","IMPRINT",EDGE,{"disambiguationData":[TD([[subQ2,1.0]])],"derivedFrom":subQ1}),-1.0]])]});}
            var Q66;
            {var subQ0=sQuery(id+"F0.wireOp",EDGE,"E2.6.2");var subQ1=sQuery(id+"F0.wireOp",EDGE,"E0");var subQ2=makeQuery(id+"F0.imprint","INTERSECT",VERTEX,{"derivedFrom":[subQ1,subQ0]});Q66=makeQuery(id+"F0.imprint","IMPRINT",FACE,{"disambiguationData":[TD([[makeQuery(id+"F0.imprint","IMPRINT",EDGE,{"disambiguationData":[TD([[subQ2,-1.0]])],"derivedFrom":subQ1}),-1.0]])]});}
            var Q67;
            {var subQ0=sQuery(id+"F0.wireOp",EDGE,"E2.7.2");var subQ1=sQuery(id+"F0.wireOp",EDGE,"E0");var subQ2=makeQuery(id+"F0.imprint","INTERSECT",VERTEX,{"derivedFrom":[subQ1,subQ0]});Q67=makeQuery(id+"F0.imprint","IMPRINT",FACE,{"disambiguationData":[TD([[makeQuery(id+"F0.imprint","IMPRINT",EDGE,{"disambiguationData":[TD([[subQ2,-1.0]])],"derivedFrom":subQ1}),-1.0]])]});}
            var Q68;
            {var subQ0=sQuery(id+"F0.wireOp",EDGE,"E2.5.2");var subQ1=sQuery(id+"F0.wireOp",EDGE,"E0");var subQ2=makeQuery(id+"F0.imprint","INTERSECT",VERTEX,{"derivedFrom":[subQ1,subQ0]});Q68=makeQuery(id+"F0.imprint","IMPRINT",FACE,{"disambiguationData":[TD([[makeQuery(id+"F0.imprint","IMPRINT",EDGE,{"disambiguationData":[TD([[subQ2,-1.0]])],"derivedFrom":subQ1}),-1.0]])]});}
            var Q69;
            {var subQ0=sQuery(id+"F0.wireOp",EDGE,"E2.4.2");var subQ1=sQuery(id+"F0.wireOp",EDGE,"E0");var subQ2=makeQuery(id+"F0.imprint","INTERSECT",VERTEX,{"derivedFrom":[subQ1,subQ0]});Q69=makeQuery(id+"F0.imprint","IMPRINT",FACE,{"disambiguationData":[TD([[makeQuery(id+"F0.imprint","IMPRINT",EDGE,{"disambiguationData":[TD([[subQ2,-1.0]])],"derivedFrom":subQ1}),-1.0]])]});}
            var Q70;
            {var subQ0=sQuery(id+"F0.wireOp",EDGE,"E2.3.2");var subQ1=sQuery(id+"F0.wireOp",EDGE,"E0");var subQ2=makeQuery(id+"F0.imprint","INTERSECT",VERTEX,{"derivedFrom":[subQ1,subQ0]});Q70=makeQuery(id+"F0.imprint","IMPRINT",FACE,{"disambiguationData":[TD([[makeQuery(id+"F0.imprint","IMPRINT",EDGE,{"disambiguationData":[TD([[subQ2,-1.0]])],"derivedFrom":subQ1}),-1.0]])]});}
            var Q71;
            {var subQ0=sQuery(id+"F0.wireOp",EDGE,"E2.2.2");var subQ1=sQuery(id+"F0.wireOp",EDGE,"E0");var subQ2=makeQuery(id+"F0.imprint","INTERSECT",VERTEX,{"derivedFrom":[subQ1,subQ0]});Q71=makeQuery(id+"F0.imprint","IMPRINT",FACE,{"disambiguationData":[TD([[makeQuery(id+"F0.imprint","IMPRINT",EDGE,{"disambiguationData":[TD([[subQ2,-1.0]])],"derivedFrom":subQ1}),-1.0]])]});}
            extrude(context, id + "F1", {"entities" : qUnion([Q0, Q1, Q2, Q3, Q4, Q5, Q6, Q7, Q8, Q9, Q10, Q11, Q12, Q13, Q14, Q15, Q16, Q17, Q18, Q19, Q20, Q21, Q22, Q23, Q24, Q25, Q26, Q27, Q28, Q29, Q30, Q31, Q32, Q33, Q34, Q35, Q36, Q37, Q38, Q39, Q40, Q41, Q42, Q43, Q44, Q45, Q46, Q47, Q48, Q49, Q50, Q51, Q52, Q53, Q54, Q55, Q56, Q57, Q58, Q59, Q60, Q61, Q62, Q63, Q64, Q65, Q66, Q67, Q68, Q69, Q70, Q71]), "endBound" : BoundingType.SYMMETRIC, "depth" : 2.7 * mm, "offsetDistance" : 25 * mm});
        }
        {
            var Q0;
            Q0=qCreatedBy(makeId("Top.planeOp"),FACE);
            var sketch = newSketch(context, id + "F2", { "sketchPlane" : qUnion([Q0])});
            skCircle(sketch, "E5", {"center": v(0, 0) * mm, "radius": 0.75 * mm});
            skSolve(sketch);
        }
        {
            var Q0;
            Q0 = qSketchRegion(id + "F2", true);
            extrude(context, id + "F3", {"entities" : qUnion([Q0]), "operationType" : NewBodyOperationType.ADD, "endBound" : BoundingType.SYMMETRIC, "depth" : 12 * mm, "offsetDistance" : 25 * mm});
        }
    });
